# Revit family: 0043238 Sylvania Lighting Fixture SYLCIRCLE DIM DUAL TONE 18W 3000K 4000K
name_source: partatom
category: Lighting Fixtures
revit_build: Autodesk Revit 2016 (Build: 20150220_1215(x64)
units: mm (PartAtom-declared; Revit-internal decimal feet)

## family parameters
Cut with Voids When Loaded = No
Host = Face
Light Source = Yes
OmniClass Number = 23.80.70.11.17
OmniClass Title = Specialized Lighting by Location or Use
Part Type = Normal
Room Calculation Point = No
Round Connector Dimension = Use Diameter
Shared = No

## types (2) — shared parameters
Apparent Load = 18 VA
Assembly Code = D5020200
AssetType = Fixed
Color Filter = 16777215
Description = SYLCIRCLE DIM DUAL TONE 18W with choice of 3000K or 4000K
Diameter_FEILO = 330 mm
Dimming Lamp Color Temperature Shift = <None>
DimmingControlOptions = Dimmable
DocumentationLiterature = http://www.sylvania-lighting.com
DurationUnit = hours
ElectricShockClassification = Class I
ExpectedLife = 50000
Height_FEILO = 96 mm
IfcExportAs = IfcLightFixtureType
IfcExportType = IfcLightFixtureType
ImpactProtectionIndex = IK03
IngressProtection = IP44
InputNominalFrequency = 50 Hz
InputVoltage = 220-240V~
Keynote = 16500
Lamp = LED
LampColourRenderingIndex = 80
LampMacAdamStep = 6
LampNominalLuminous = 1500 lm
LampsType = LED
LuminousEfficacy = 83 lm/W
Manufacturer = Feilo Sylvania
ManufacturerName = Feilo Sylvania
Material = aluminium housing, pmma diffuser
Material_1_FEILO = <By Category>
Material_2_FEILO = Metal_Sylvania_Sylcircle_White
Material_3_FEILO = Polycarbonate_Sylvania_Sylcircle_Opal
Material_4_FEILO = <By Category>
Model = SYLCIRCLE DIM DUAL TONE 18W 3000K/4000K
ModelNumber = 0043238
ModelReference = SYLCIRCLE DIM DUAL TONE 18W 3000K/4000K
Name = SYLCIRCLE DIM DUAL TONE 18W 3000K/4000K
NominalHeight = 96 mm
NominalLength = 330 mm
PowerConsumption = 18 W
PowerFactor = 0.8
Radius_FEILO = 165 mm
Tilt Angle = -90°
URL = http://www.sylvania-lighting.com
Voltage = 230 V
Weight = 3.0 kg
zero-valued in all types: Default Elevation, NominalWidth

## per-type parameters (varying)
| type | LampColourTemperature | Photometric Web File | TypeName |
| 0043238 SYLCIRCLE DIM DUAL TONE 18W 3000K | 3000 K | 0043238.ies | SYLCIRCLE DIM DUAL TONE 18W 3000K |
| 0043238 SYLCIRCLE DIM DUAL TONE 18W 4000K | 4000 K | 0043238 SYLCIRCLE DIM DUAL TONE 18W 4000K.IES | SYLCIRCLE DIM DUAL TONE 18W 4000K |

## geometry (parser evidence)
native form markers: Blend x4, Sweep x3
no freeform markers — native parametric forms only
